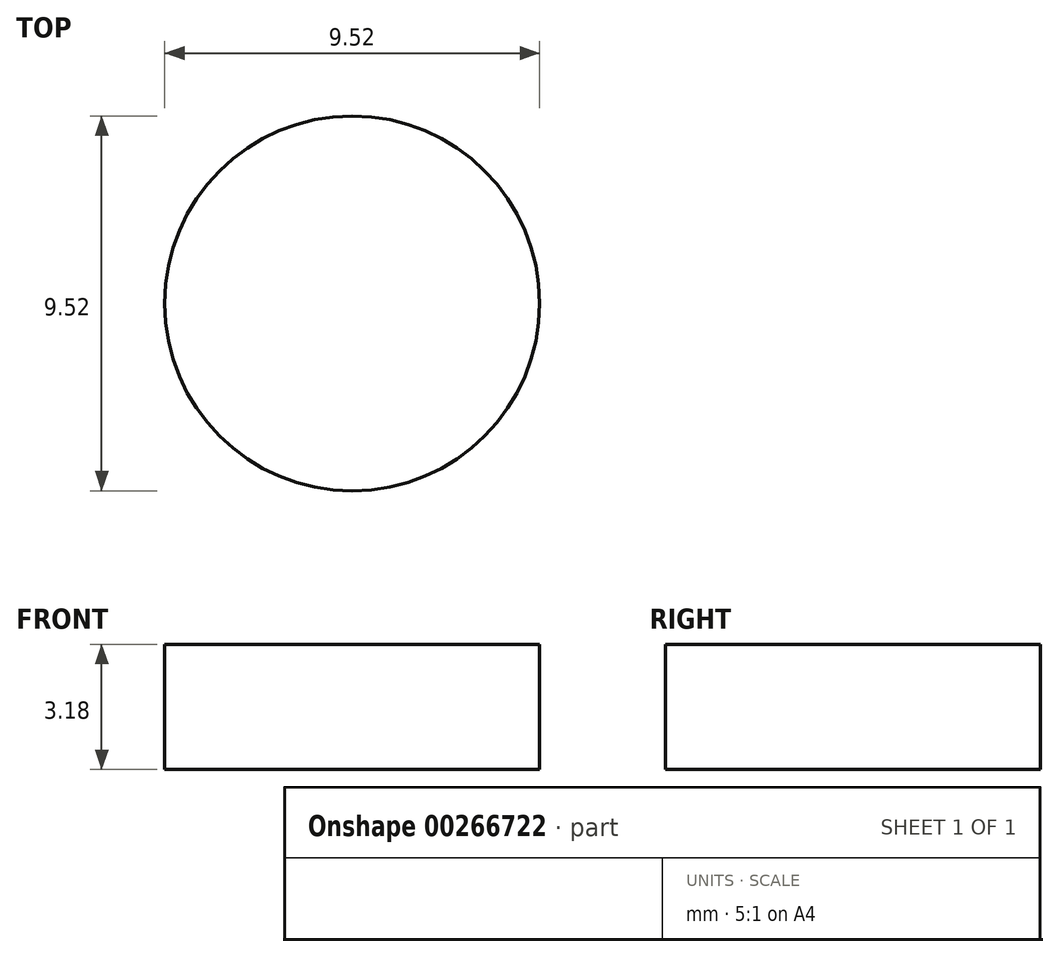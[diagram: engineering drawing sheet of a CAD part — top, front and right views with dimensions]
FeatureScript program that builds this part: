
annotation { "Feature Type Name" : "Feature", "Feature Type Description" : "" }
export const myFeature = defineFeature(function(context is Context, id is Id, definition is map)
    precondition{}
    {
        {
            var Q0;
            Q0=qCreatedBy(makeId("Top.planeOp"),FACE);
            var sketch = newSketch(context, id + "F0", { "sketchPlane" : qUnion([Q0])});
            skCircle(sketch, "E0", {"center": v(0, 0) * mm, "radius": 4.76 * mm});
            skSolve(sketch);
        }
        {
            var Q0;
            Q0=makeQuery(id+"F0.imprint","IMPRINT",FACE,{"disambiguationData":[TD([[makeQuery(id+"F0.imprint","IMPRINT",EDGE,{"derivedFrom":sQuery(id+"F0.wireOp",EDGE,"E0")}),1.0]])]});
            extrude(context, id + "F1", {"entities" : qUnion([Q0]), "depth" : 3.17 * mm});
        }
    });
